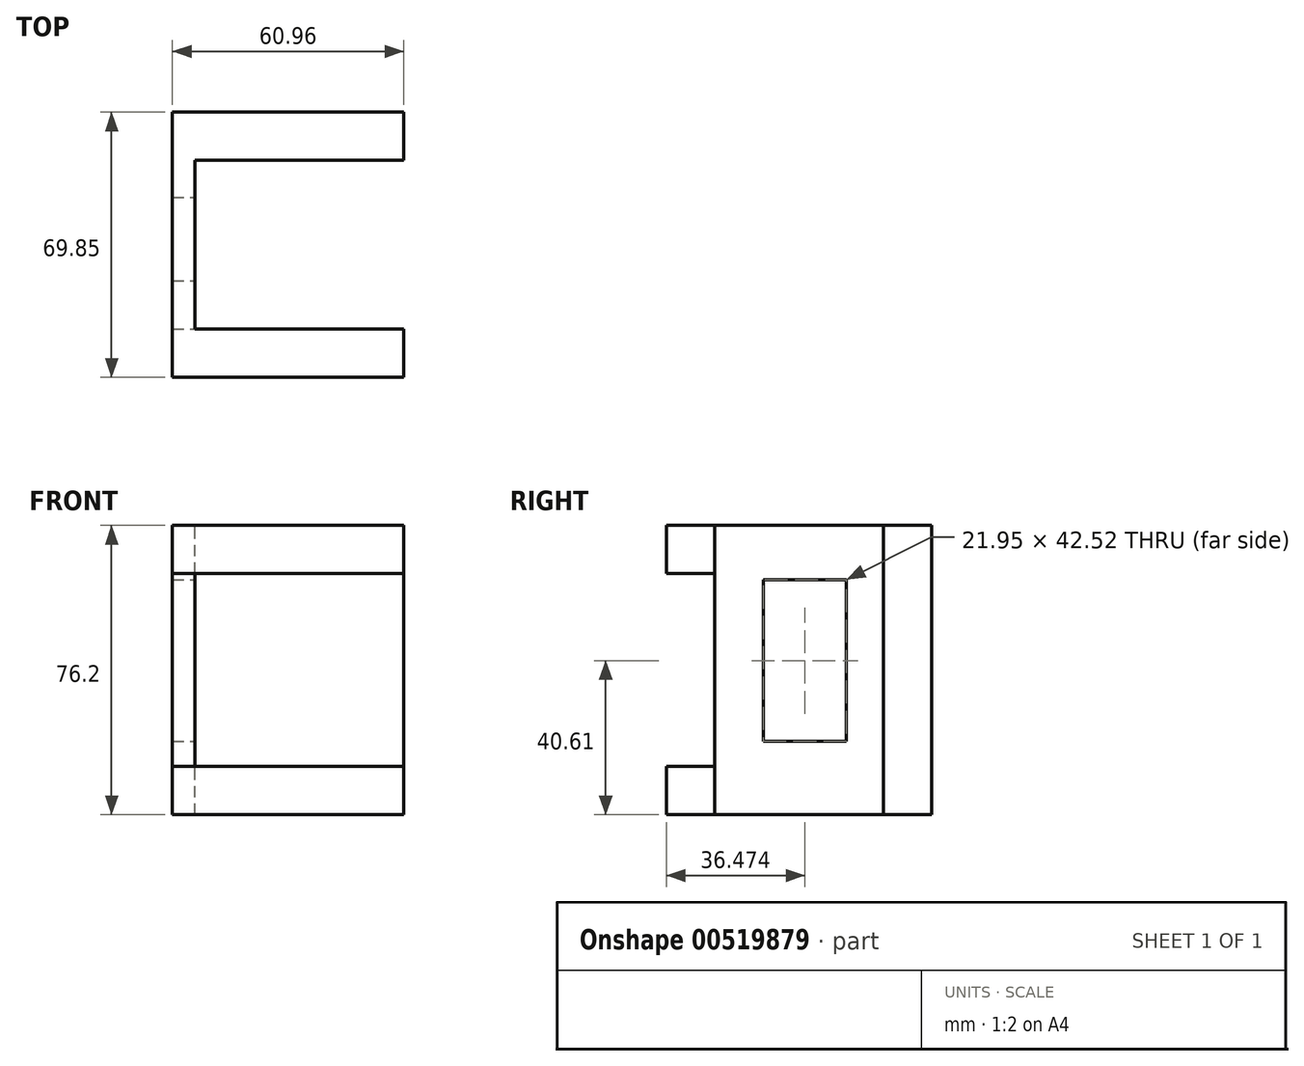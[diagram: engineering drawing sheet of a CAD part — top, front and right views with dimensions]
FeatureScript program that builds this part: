
annotation { "Feature Type Name" : "Feature", "Feature Type Description" : "" }
export const myFeature = defineFeature(function(context is Context, id is Id, definition is map)
    precondition{}
    {
        {
            var Q0;
            Q0=qCreatedBy(makeId("Front.planeOp"),FACE);
            var sketch = newSketch(context, id + "F0", { "sketchPlane" : qUnion([Q0])});
            skLineSegment(sketch, "E0.bottom", {"start": v(-34.75, -19.35) * mm, "end": v(26.21, -19.35) * mm});
            skLineSegment(sketch, "E0.top", {"start": v(-34.75, 56.85) * mm, "end": v(26.21, 56.85) * mm});
            skLineSegment(sketch, "E0.left", {"start": v(-34.75, -19.35) * mm, "end": v(-34.75, 56.85) * mm});
            skLineSegment(sketch, "E0.right", {"start": v(26.21, -19.35) * mm, "end": v(26.21, 56.85) * mm});
            skSolve(sketch);
        }
        {
            var Q0;
            Q0=makeQuery(id+"F0.imprint","IMPRINT",FACE,{"disambiguationData":[TD([[makeQuery(id+"F0.imprint","IMPRINT",EDGE,{"derivedFrom":sQuery(id+"F0.wireOp",EDGE,"E0.bottom")}),1.0]])]});
            extrude(context, id + "F1", {"entities" : qUnion([Q0]), "depth" : 12.7 * mm, "offsetDistance" : 25.4 * mm});
        }
        {
            var Q0;
            Q0=makeQuery(id+"F1.opExtrude","CAP_FACE",FACE,{"disambiguationData":[OSD([sQuery(id+"F0.wireOp",EDGE,"E0.bottom"),sQuery(id+"F0.wireOp",EDGE,"E0.top"),sQuery(id+"F0.wireOp",EDGE,"E0.left"),sQuery(id+"F0.wireOp",EDGE,"E0.right")])],"isStart":true});
            var sketch = newSketch(context, id + "F2", { "sketchPlane" : qUnion([Q0])});
            skLineSegment(sketch, "E1.bottom", {"start": v(34.75, -19.35) * mm, "end": v(28.8, -19.35) * mm});
            skLineSegment(sketch, "E1.top", {"start": v(34.75, 56.85) * mm, "end": v(28.8, 56.85) * mm});
            skLineSegment(sketch, "E1.left", {"start": v(34.75, -19.35) * mm, "end": v(34.75, 56.85) * mm});
            skLineSegment(sketch, "E1.right", {"start": v(28.8, -19.35) * mm, "end": v(28.8, 56.85) * mm});
            skSolve(sketch);
        }
        {
            var Q0;
            Q0=makeQuery(id+"F2.imprint","IMPRINT",FACE,{"disambiguationData":[TD([[makeQuery(id+"F2.imprint","IMPRINT",EDGE,{"derivedFrom":sQuery(id+"F2.wireOp",EDGE,"E1.bottom")}),-1.0]])]});
            extrude(context, id + "F3", {"entities" : qUnion([Q0]), "operationType" : NewBodyOperationType.ADD, "depth" : 57.15 * mm, "offsetDistance" : 25.4 * mm});
        }
        {
            var Q0;
            Q0=makeQuery(id+"F3.opExtrude","SWEPT_FACE",FACE,{"disambiguationData":[OSD([sQuery(id+"F2.wireOp",EDGE,"E1.right")])]});
            var sketch = newSketch(context, id + "F4", { "sketchPlane" : qUnion([Q0])});
            skLineSegment(sketch, "E2.bottom", {"start": v(57.15, -19.35) * mm, "end": v(44.45, -19.35) * mm});
            skLineSegment(sketch, "E2.top", {"start": v(57.15, 56.85) * mm, "end": v(44.45, 56.85) * mm});
            skLineSegment(sketch, "E2.left", {"start": v(57.15, -19.35) * mm, "end": v(57.15, 56.85) * mm});
            skLineSegment(sketch, "E2.right", {"start": v(44.45, -19.35) * mm, "end": v(44.45, 56.85) * mm});
            skSolve(sketch);
        }
        {
            var Q0;
            Q0 = qSketchRegion(id + "F4", true);
            extrude(context, id + "F5", {"entities" : qUnion([Q0]), "operationType" : NewBodyOperationType.ADD, "depth" : 55.02 * mm, "offsetDistance" : 25.4 * mm});
        }
        {
            var Q0;
            Q0=makeQuery(id+"F1.opExtrude","SWEPT_FACE",FACE,{"disambiguationData":[OSD([sQuery(id+"F0.wireOp",EDGE,"E0.right")])]});
            var sketch = newSketch(context, id + "F6", { "sketchPlane" : qUnion([Q0])});
            skLineSegment(sketch, "E3.bottom", {"start": v(-12.7, 44.15) * mm, "end": v(0, 44.15) * mm});
            skLineSegment(sketch, "E3.top", {"start": v(-12.7, -6.65) * mm, "end": v(0, -6.65) * mm});
            skLineSegment(sketch, "E3.left", {"start": v(-12.7, 44.15) * mm, "end": v(-12.7, -6.65) * mm});
            skLineSegment(sketch, "E3.right", {"start": v(0, 44.15) * mm, "end": v(0, -6.65) * mm});
            skSolve(sketch);
        }
        {
            var Q0;
            Q0=makeQuery(id+"F6.imprint","IMPRINT",FACE,{"disambiguationData":[TD([[makeQuery(id+"F6.imprint","IMPRINT",EDGE,{"derivedFrom":sQuery(id+"F6.wireOp",EDGE,"E3.bottom")}),-1.0]])]});
            var Q1;
            Q1 = qSketchRegion(id + "F6", true);
            extrude(context, id + "F7", {"entities" : qUnion([Q0, Q1]), "operationType" : NewBodyOperationType.REMOVE, "oppositeDirection" : true, "depth" : 63.5 * mm, "offsetDistance" : 25.4 * mm});
        }
        {
            var Q0;
            {var subQ0=sQuery(id+"F4.wireOp",EDGE,"E2.right");Q0=makeQuery(id+"F4.imprint","IMPRINT",FACE,{"disambiguationData":[TD([[makeQuery(id+"F4.imprint","IMPRINT",EDGE,{"derivedFrom":subQ0}),1.0]])]});}
            var sketch = newSketch(context, id + "F8", { "sketchPlane" : qUnion([Q0])});
            skLineSegment(sketch, "E4.bottom", {"start": v(12.8, 0) * mm, "end": v(34.75, 0) * mm});
            skLineSegment(sketch, "E4.top", {"start": v(12.8, 42.52) * mm, "end": v(34.75, 42.52) * mm});
            skLineSegment(sketch, "E4.left", {"start": v(12.8, 0) * mm, "end": v(12.8, 42.52) * mm});
            skLineSegment(sketch, "E4.right", {"start": v(34.75, 0) * mm, "end": v(34.75, 42.52) * mm});
            skSolve(sketch);
        }
        {
            var Q0;
            Q0=makeQuery(id+"F8.imprint","IMPRINT",FACE,{"disambiguationData":[TD([[makeQuery(id+"F8.imprint","IMPRINT",EDGE,{"derivedFrom":sQuery(id+"F8.wireOp",EDGE,"E4.bottom")}),1.0]])]});
            extrude(context, id + "F9", {"entities" : qUnion([Q0]), "operationType" : NewBodyOperationType.REMOVE, "oppositeDirection" : true, "depth" : 25.4 * mm, "offsetDistance" : 25.4 * mm});
        }
    });
